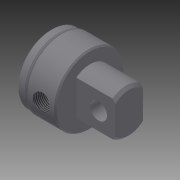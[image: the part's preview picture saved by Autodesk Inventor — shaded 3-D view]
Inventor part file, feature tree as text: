
AUTODESK INVENTOR PART (.ipt)
format: ipt  version: 2014 (Build 180170000, 170)  size: 254,976 bytes
history: native  units: in
note: dims shown in document units (in); Inventor stores cm internally (conversion verified against a paired STEP export)
features: other x126, sketch x8, revolve x5, extrude x2, hole x1, thread x1
ambient origin geometry x8: Origin, YZ Plane, XZ Plane, XY Plane, X Axis, Y Axis, Z Axis, Center Point
bodies: Solid1 (feature_tree)
feature tree (143):
  revolve  "Revolution1"  Angle=360.0deg
  revolve  "Revolution2"  Angle=360.0deg
  extrude  "Extrusion1"  TaperAngle=360.0deg  [1 undecoded]
  hole  "Hole1"  [1 undecoded]
  revolve  "Revolution3"  [1 undecoded]
  thread  "Thread1"  [1 undecoded]
  revolve  "Revolution4"  [1 undecoded]
  revolve  "Revolution5"  [1 undecoded]
  extrude  "Extrusion2"  [1 undecoded]
  other  "f_XY"
  other  "f_YZ"
  other  "f_ZX"
  other  "f_X"
  other  "f_Y"
  other  "f_Z"
  other  "f_Center"
  other  "lovra1_XY"
  other  "lovra1_YZ"
  other  "lovra1_ZX"
  other  "lovra1_X"
  other  "lovra1_Y"
  other  "lovra1_Z"
  other  "lovra1_Center"
  other  "lovra2_XY"
  other  "lovra2_YZ"
  other  "lovra2_ZX"
  other  "lovra2_X"
  other  "lovra2_Y"
  other  "lovra2_Z"
  other  "lovra2_Center"
  other  "lovra21_XY"
  other  "lovra21_YZ"
  other  "lovra21_ZX"
  other  "lovra21_X"
  other  "lovra21_Y"
  other  "lovra21_Z"
  other  "lovra21_Center"
  other  "lovra22_XY"
  other  "lovra22_YZ"
  other  "lovra22_ZX"
  other  "lovra22_X"
  other  "lovra22_Y"
  other  "lovra22_Z"
  other  "lovra22_Center"
  other  "lovra3_XY"
  other  "lovra3_YZ"
  other  "lovra3_ZX"
  other  "lovra3_X"
  other  "lovra3_Y"
  other  "lovra3_Z"
  other  "lovra3_Center"
  other  "olen_XY"
  other  "olen_YZ"
  other  "olen_ZX"
  other  "olen_X"
  other  "olen_Y"
  other  "olen_Z"
  other  "olen_Center"
  other  "p1_XY"
  other  "p1_YZ"
  other  "p1_ZX"
  other  "p1_X"
  other  "p1_Y"
  other  "p1_Z"
  other  "p1_Center"
  other  "p2_XY"
  other  "p2_YZ"
  other  "p2_ZX"
  other  "p2_X"
  other  "p2_Y"
  other  "p2_Z"
  other  "p2_Center"
  other  "port_XY"
  other  "port_YZ"
  other  "port_ZX"
  other  "port_X"
  other  "port_Y"
  other  "port_Z"
  other  "port_Center"
  other  "port2_XY"
  other  "port2_YZ"
  other  "port2_ZX"
  other  "port2_X"
  other  "port2_Y"
  other  "port2_Z"
  other  "port2_Center"
  other  "thd1_XY"
  other  "thd1_YZ"
  other  "thd1_ZX"
  other  "thd1_X"
  other  "thd1_Y"
  other  "thd1_Z"
  other  "thd1_Center"
  other  "thd2_XY"
  other  "thd2_YZ"
  other  "thd2_ZX"
  other  "thd2_X"
  other  "thd2_Y"
  other  "thd2_Z"
  other  "thd2_Center"
  other  "to_mounting_bracket_XY"
  other  "to_mounting_bracket_YZ"
  other  "to_mounting_bracket_ZX"
  other  "to_mounting_bracket_X"
  other  "to_mounting_bracket_Y"
  other  "to_mounting_bracket_Z"
  other  "to_mounting_bracket_Center"
  other  "to_nut_XY"
  other  "to_nut_YZ"
  other  "to_nut_ZX"
  other  "to_nut_X"
  other  "to_nut_Y"
  other  "to_nut_Z"
  other  "to_nut_Center"
  other  "to_pin_XY"
  other  "to_pin_YZ"
  other  "to_pin_ZX"
  other  "to_pin_X"
  other  "to_pin_Y"
  other  "to_pin_Z"
  other  "to_pin_Center"
  other  "to_screw_XY"
  other  "to_screw_YZ"
  other  "to_screw_ZX"
  other  "to_screw_X"
  other  "to_screw_Y"
  other  "to_screw_Z"
  other  "to_screw_Center"
  other  "to_tube_XY"
  other  "to_tube_YZ"
  other  "to_tube_ZX"
  other  "to_tube_X"
  other  "to_tube_Y"
  other  "to_tube_Z"
  other  "to_tube_Center"
  sketch  "Sketch_18"  dims[d4=0.532in d5=0.75in d6=0.375in d7=0.25in d8=0.5635in d9=0.8052in d10=120.0deg d11=360.0deg]
  sketch  "Sketch_21"  dims[d15=360.0deg d16=0.9255in d17=0.0in]
  sketch  "Sketch_9"  dims[d2=0.875in d3=0.0in]
  sketch  "Sketch4"  dims[d0=360.0deg d1=360.0deg]
  sketch  "Sketch_68"
  sketch  "Sketch_20"  dims[d12=0.2731in d13=0.0in d14=360.0deg]
  sketch  "Sketch_24"
  sketch  "Sketch_43"
note: 7 required parameter values undecoded (feature->parameter linkage not recoverable at this tier; creation-order binding heuristic only, values carry confidence <= 0.55)
